# Revit family: Plumbing-Fix_Flush-Valve_Stern_Venus-PE
name_source: partatom
category: Plumbing Fixtures
units: mm (PartAtom-declared; Revit-internal decimal feet)

## family parameters
Classification Number = 23.45.05.14
Cut with Voids When Loaded = No
Enable Cutting in Views = No
Host = Face
Maintain Annotation Orientation = No
Part Type = Normal
Room Calculation Point = No
Round Connector Dimension = Use Diameter
Shared = No

## types (1)
- as Specified
    Assembly Code = D2010300
    Available Options = as Specified
    Body Construction = Brass
    CW Connection = Yes
    CWFU = 1
    Cost = 0 $
    Default Elevation = 0' - 0"
    Description = Stern High Security Flush Valve - Venus 3003R PE as Specified
    Expected Lifespan (Years) = 0
    GPF = 1.6
    HW Connection = No
    HWFU = 0
    Maintenance Schedule (Months) = 0
    Manufacturer = Stern Engineering
    Manufacturer Website = http://www.sternfaucets.com
    Model = Venus 3003R PE
    Operating Pressure Range = 7.26 - 116 PSI  ;  0.5 - 8 bar
    Operating Temperature Range = as Specified
    Piping_Flow = 0 GPM
    Piping_Inlet Diameter = 1"
    Power Supply = 9V Transformer
    Product Data = http://www.arcat.com
    Product Features = Flushing Piezo Element Separate from Valve
    Revision = R1_2018-04
    Sales Information = http://www.sternfaucets.com
    Standards Conformance = as Specified
    Type Comments = as Specified
    URL = http://www.sternfaucets.com
    Unit Height = 1' - 3 3/4"
    Unit Width = 0' - 7 1/2"
    Vent Connection = No
    WFU = 0
    Warranty Duration (Years) = 2
    Waste Connection = No

## geometry (parser evidence)
native form markers: Sweep x2
no freeform markers — native parametric forms only
